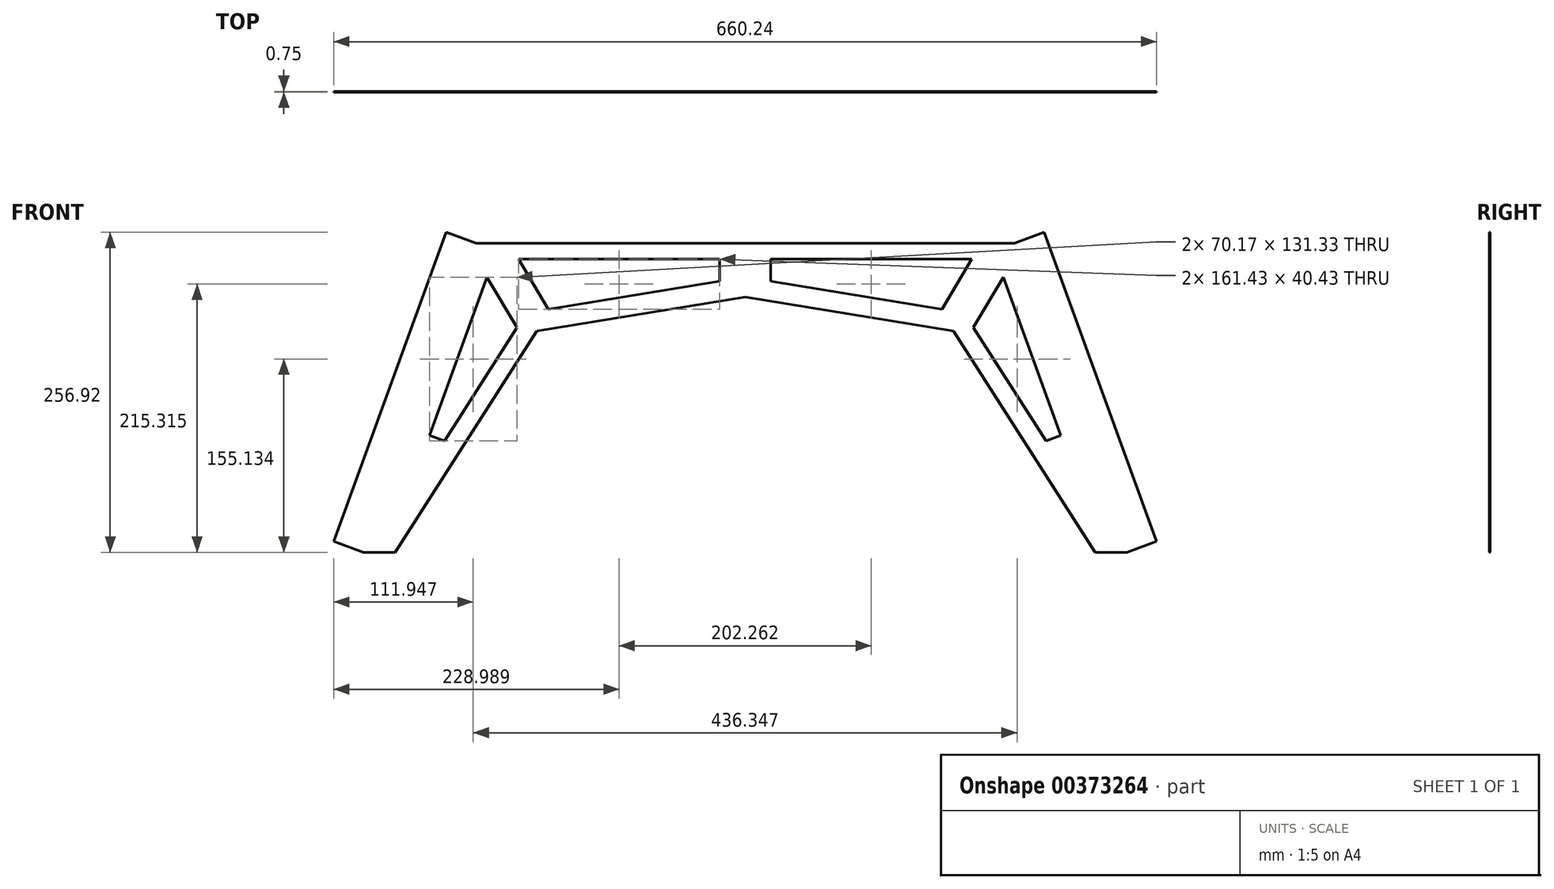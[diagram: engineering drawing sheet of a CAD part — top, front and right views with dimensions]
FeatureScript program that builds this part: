
annotation { "Feature Type Name" : "Feature", "Feature Type Description" : "" }
export const myFeature = defineFeature(function(context is Context, id is Id, definition is map)
    precondition{}
    {
        {
            assignVariable(context, id + "F0", {"name" : "ply", "anyValue" : .75});
        }
        {
            var Q0;
            Q0=qCreatedBy(makeId("Front.planeOp"),FACE);
            var sketch = newSketch(context, id + "F1", { "sketchPlane" : qUnion([Q0])});
            skLineSegment(sketch, "E0", {"start": v(0, 0) * mm, "end": v(-215.9, 0) * mm});
            skLineSegment(sketch, "E1", {"start": v(-215.9, 0) * mm, "end": v(-306.25, -248.23) * mm});
            skLineSegment(sketch, "E2.MirrorCS", {"start": v(0, 0) * mm, "end": v(215.9, 0) * mm});
            skLineSegment(sketch, "E3.MirrorCS", {"start": v(215.9, 0) * mm, "end": v(306.25, -248.23) * mm});
            skLineSegment(sketch, "E4", {"start": v(-306.25, -248.23) * mm, "end": v(-280.85, -248.23) * mm});
            skLineSegment(sketch, "E5", {"start": v(-280.85, -248.23) * mm, "end": v(-167.13, -70.71) * mm});
            skLineSegment(sketch, "E6", {"start": v(-167.13, -70.71) * mm, "end": v(0, -43.18) * mm});
            skLineSegment(sketch, "E7.MirrorCS", {"start": v(167.13, -70.71) * mm, "end": v(0, -43.18) * mm});
            skLineSegment(sketch, "E8.MirrorCS", {"start": v(280.85, -248.23) * mm, "end": v(167.13, -70.71) * mm});
            skLineSegment(sketch, "E9.MirrorCS", {"start": v(306.25, -248.23) * mm, "end": v(280.85, -248.23) * mm});
            skLineSegment(sketch, "E10", {"start": v(-20.41, -12.7) * mm, "end": v(-20.41, -30.48) * mm});
            skLineSegment(sketch, "E11", {"start": v(-20.41, -30.48) * mm, "end": v(-157.9, -53.13) * mm});
            skLineSegment(sketch, "E12", {"start": v(-157.9, -53.13) * mm, "end": v(-181.85, -12.7) * mm});
            skLineSegment(sketch, "E13", {"start": v(-181.85, -12.7) * mm, "end": v(-20.41, -12.7) * mm});
            skLineSegment(sketch, "E14", {"start": v(-207.04, -27.43) * mm, "end": v(-183.1, -67.86) * mm});
            skLineSegment(sketch, "E15", {"start": v(-183.1, -67.86) * mm, "end": v(-241.32, -158.76) * mm});
            skLineSegment(sketch, "E16", {"start": v(-241.32, -158.76) * mm, "end": v(-253.26, -154.42) * mm});
            skLineSegment(sketch, "E17", {"start": v(-253.26, -154.42) * mm, "end": v(-207.04, -27.43) * mm});
            skLineSegment(sketch, "E18.MirrorCS", {"start": v(20.41, -30.48) * mm, "end": v(157.9, -53.13) * mm});
            skLineSegment(sketch, "E19.MirrorCS", {"start": v(181.85, -12.7) * mm, "end": v(20.41, -12.7) * mm});
            skLineSegment(sketch, "E20.MirrorCS", {"start": v(157.9, -53.13) * mm, "end": v(181.85, -12.7) * mm});
            skLineSegment(sketch, "E21.MirrorCS", {"start": v(207.04, -27.43) * mm, "end": v(183.1, -67.86) * mm});
            skLineSegment(sketch, "E22.MirrorCS", {"start": v(253.26, -154.42) * mm, "end": v(207.04, -27.43) * mm});
            skLineSegment(sketch, "E23.MirrorCS", {"start": v(183.1, -67.86) * mm, "end": v(241.32, -158.76) * mm});
            skLineSegment(sketch, "E24.MirrorCS", {"start": v(241.32, -158.76) * mm, "end": v(253.26, -154.42) * mm});
            skLineSegment(sketch, "E25.MirrorCS", {"start": v(20.41, -12.7) * mm, "end": v(20.41, -30.48) * mm});
            skLineSegment(sketch, "E26", {"start": v(-215.9, 0) * mm, "end": v(-239.77, 8.69) * mm});
            skLineSegment(sketch, "E27", {"start": v(-239.77, 8.69) * mm, "end": v(-330.12, -239.54) * mm});
            skLineSegment(sketch, "E28", {"start": v(-330.12, -239.54) * mm, "end": v(-306.25, -248.23) * mm});
            skLineSegment(sketch, "E29.MirrorCS", {"start": v(239.77, 8.69) * mm, "end": v(330.12, -239.54) * mm});
            skLineSegment(sketch, "E30.MirrorCS", {"start": v(215.9, 0) * mm, "end": v(239.77, 8.69) * mm});
            skLineSegment(sketch, "E31.MirrorCS", {"start": v(330.12, -239.54) * mm, "end": v(306.25, -248.23) * mm});
            skSolve(sketch);
        }
        {
            var Q0;
            Q0=makeQuery(id+"F1.imprint","IMPRINT",FACE,{"disambiguationData":[TD([[makeQuery(id+"F1.imprint","IMPRINT",EDGE,{"derivedFrom":sQuery(id+"F1.wireOp",EDGE,"E0")}),1.0]])]});
            var Q1;
            Q1=makeQuery(id+"F1.imprint","IMPRINT",FACE,{"disambiguationData":[TD([[makeQuery(id+"F1.imprint","IMPRINT",EDGE,{"derivedFrom":sQuery(id+"F1.wireOp",EDGE,"E1")}),-1.0]])]});
            var Q2;
            Q2=makeQuery(id+"F1.imprint","IMPRINT",FACE,{"disambiguationData":[TD([[makeQuery(id+"F1.imprint","IMPRINT",EDGE,{"derivedFrom":sQuery(id+"F1.wireOp",EDGE,"E3.MirrorCS")}),1.0]])]});
            extrude(context, id + "F2", {"entities" : qUnion([Q0, Q1, Q2]), "depth" : (getVariable(context, 'ply')) * mm});
        }
    });
